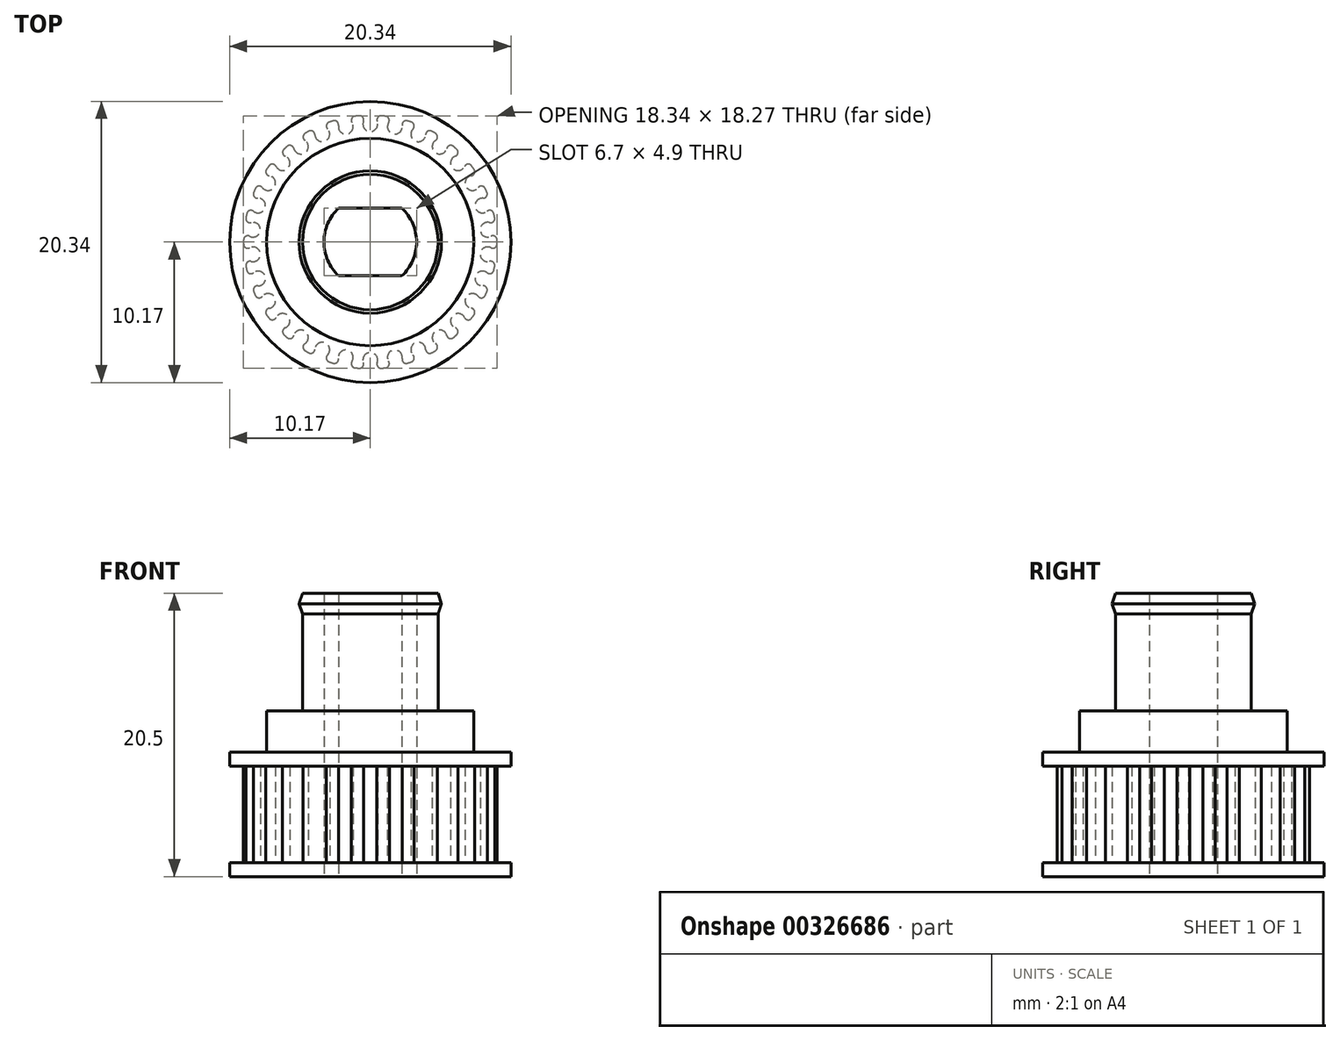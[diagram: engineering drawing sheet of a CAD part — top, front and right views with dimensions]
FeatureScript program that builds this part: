
annotation { "Feature Type Name" : "Feature", "Feature Type Description" : "" }
export const myFeature = defineFeature(function(context is Context, id is Id, definition is map)
    precondition{}
    {
        {
            assignVariable(context, id + "F0", {"name" : "e", "anyValue" : 3});
        }
        {
            assignVariable(context, id + "F1", {"name" : "h1", "anyValue" : 6});
        }
        {
            assignVariable(context, id + "F2", {"name" : "h2", "anyValue" : 6.5 + 5});
        }
        {
            var Q0;
            Q0=qCreatedBy(makeId("Top.planeOp"),FACE);
            var sketch = newSketch(context, id + "F3", { "sketchPlane" : qUnion([Q0])});
            skArc(sketch, "E0", {"start": v(-0.8, 9.13) * mm, "mid": v(0, -9.17) * mm, "end": v(0.8, 9.13) * mm, "construction": true});
            skCircle(sketch, "E1", {"center": v(0, 0) * mm, "radius": 7.5 * mm});
            skCircle(sketch, "E2", {"center": v(0, 0) * mm, "radius": 4.9 * mm});
            skArc(sketch, "E3", {"start": v(-2.28, 2.45) * mm, "mid": v(-3.35, 0) * mm, "end": v(-2.28, -2.45) * mm});
            skLineSegment(sketch, "E4.bottom", {"start": v(2.28, -2.45) * mm, "end": v(-2.28, -2.45) * mm});
            skLineSegment(sketch, "E4.top", {"start": v(2.28, 2.45) * mm, "end": v(-2.28, 2.45) * mm});
            skArc(sketch, "E5.trimOffspring", {"start": v(2.28, -2.45) * mm, "mid": v(3.35, 0) * mm, "end": v(2.28, 2.45) * mm});
            skPoint(sketch, "E6.orphan", {"position": v(3.35, 2.45) * mm});
            skPoint(sketch, "E7.orphan", {"position": v(3.35, -2.45) * mm});
            skPoint(sketch, "E8.orphan", {"position": v(-3.35, -2.45) * mm});
            skPoint(sketch, "E9.orphan", {"position": v(-3.35, 2.45) * mm});
            skLineSegment(sketch, "E10", {"start": v(0, 7.5) * mm, "end": v(0, 8) * mm, "construction": true});
            skCircle(sketch, "E11", {"center": v(0, 0) * mm, "radius": 10.17 * mm});
            skCircle(sketch, "E12", {"center": v(0, 0) * mm, "radius": 8 * mm, "construction": true});
            skLineSegment(sketch, "E13", {"start": v(0, 8) * mm, "end": v(0, 10.17) * mm});
            skArc(sketch, "E14", {"start": v(-0.5, 8.73) * mm, "mid": v(0, 8) * mm, "end": v(0.5, 8.73) * mm});
            skArc(sketch, "E15", {"start": v(0.8, 9.13) * mm, "mid": v(0.54, 9.01) * mm, "end": v(0.5, 8.73) * mm});
            skArc(sketch, "E16.MirrorCS", {"start": v(-0.8, 9.13) * mm, "mid": v(-0.54, 9.01) * mm, "end": v(-0.5, 8.73) * mm});
            skLineSegment(sketch, "E17", {"start": v(0, 0) * mm, "end": v(1.06, 10.11) * mm, "construction": true});
            skLineSegment(sketch, "E18", {"start": v(0, 0) * mm, "end": v(-1.06, 10.11) * mm, "construction": true});
            skArc(sketch, "E19", {"start": v(0.96, 9.12) * mm, "mid": v(0.88, 9.13) * mm, "end": v(0.8, 9.13) * mm});
            skArc(sketch, "E20.trimOffspring", {"start": v(-0.8, 9.13) * mm, "mid": v(-0.88, 9.13) * mm, "end": v(-0.96, 9.12) * mm});
            skArc(sketch, "E21.1.0", {"start": v(-2.69, 8.77) * mm, "mid": v(-2.76, 8.74) * mm, "end": v(-2.83, 8.72) * mm});
            skArc(sketch, "E21.1.1", {"start": v(-2.69, 8.77) * mm, "mid": v(-2.4, 8.7) * mm, "end": v(-2.3, 8.43) * mm});
            skArc(sketch, "E21.1.2", {"start": v(-2.3, 8.43) * mm, "mid": v(-1.66, 7.82) * mm, "end": v(-1.33, 8.64) * mm});
            skArc(sketch, "E21.1.3", {"start": v(-1.11, 9.1) * mm, "mid": v(-1.35, 8.93) * mm, "end": v(-1.33, 8.64) * mm});
            skArc(sketch, "E21.1.4", {"start": v(-0.96, 9.12) * mm, "mid": v(-1.04, 9.1) * mm, "end": v(-1.11, 9.1) * mm});
            skArc(sketch, "E21.2.0", {"start": v(-4.45, 8.02) * mm, "mid": v(-4.52, 7.98) * mm, "end": v(-4.58, 7.94) * mm});
            skArc(sketch, "E21.2.1", {"start": v(-4.45, 8.02) * mm, "mid": v(-4.16, 8.02) * mm, "end": v(-4, 7.77) * mm});
            skArc(sketch, "E21.2.2", {"start": v(-4, 7.77) * mm, "mid": v(-3.25, 7.3) * mm, "end": v(-3.1, 8.17) * mm});
            skArc(sketch, "E21.2.3", {"start": v(-2.98, 8.67) * mm, "mid": v(-3.17, 8.45) * mm, "end": v(-3.1, 8.17) * mm});
            skArc(sketch, "E21.2.4", {"start": v(-2.83, 8.72) * mm, "mid": v(-2.9, 8.7) * mm, "end": v(-2.98, 8.67) * mm});
            skArc(sketch, "E21.3.0", {"start": v(-6.02, 6.92) * mm, "mid": v(-6.08, 6.86) * mm, "end": v(-6.13, 6.81) * mm});
            skArc(sketch, "E21.3.1", {"start": v(-6.02, 6.92) * mm, "mid": v(-5.73, 6.98) * mm, "end": v(-5.53, 6.77) * mm});
            skArc(sketch, "E21.3.2", {"start": v(-5.53, 6.77) * mm, "mid": v(-4.7, 6.47) * mm, "end": v(-4.73, 7.35) * mm});
            skArc(sketch, "E21.3.3", {"start": v(-4.72, 7.86) * mm, "mid": v(-4.86, 7.6) * mm, "end": v(-4.73, 7.35) * mm});
            skArc(sketch, "E21.3.4", {"start": v(-4.58, 7.94) * mm, "mid": v(-4.65, 7.9) * mm, "end": v(-4.72, 7.86) * mm});
            skArc(sketch, "E21.4.0", {"start": v(-7.33, 5.51) * mm, "mid": v(-7.37, 5.45) * mm, "end": v(-7.42, 5.39) * mm});
            skArc(sketch, "E21.4.1", {"start": v(-7.33, 5.51) * mm, "mid": v(-7.06, 5.63) * mm, "end": v(-6.82, 5.47) * mm});
            skArc(sketch, "E21.4.2", {"start": v(-6.82, 5.47) * mm, "mid": v(-5.94, 5.35) * mm, "end": v(-6.15, 6.2) * mm});
            skArc(sketch, "E21.4.3", {"start": v(-6.25, 6.7) * mm, "mid": v(-6.34, 6.43) * mm, "end": v(-6.15, 6.2) * mm});
            skArc(sketch, "E21.4.4", {"start": v(-6.13, 6.81) * mm, "mid": v(-6.2, 6.76) * mm, "end": v(-6.25, 6.7) * mm});
            skArc(sketch, "E21.5.0", {"start": v(-8.31, 3.87) * mm, "mid": v(-8.34, 3.8) * mm, "end": v(-8.38, 3.73) * mm});
            skArc(sketch, "E21.5.1", {"start": v(-8.31, 3.87) * mm, "mid": v(-8.08, 4.04) * mm, "end": v(-7.8, 3.93) * mm});
            skArc(sketch, "E21.5.2", {"start": v(-7.8, 3.93) * mm, "mid": v(-6.93, 4) * mm, "end": v(-7.3, 4.8) * mm});
            skArc(sketch, "E21.5.3", {"start": v(-7.5, 5.26) * mm, "mid": v(-7.54, 4.97) * mm, "end": v(-7.3, 4.8) * mm});
            skArc(sketch, "E21.5.4", {"start": v(-7.42, 5.39) * mm, "mid": v(-7.46, 5.33) * mm, "end": v(-7.5, 5.26) * mm});
            skArc(sketch, "E21.6.0", {"start": v(-8.93, 2.06) * mm, "mid": v(-8.95, 1.98) * mm, "end": v(-8.97, 1.9) * mm});
            skArc(sketch, "E21.6.1", {"start": v(-8.93, 2.06) * mm, "mid": v(-8.74, 2.27) * mm, "end": v(-8.45, 2.22) * mm});
            skArc(sketch, "E21.6.2", {"start": v(-8.45, 2.22) * mm, "mid": v(-7.6, 2.47) * mm, "end": v(-8.14, 3.17) * mm});
            skArc(sketch, "E21.6.3", {"start": v(-8.44, 3.59) * mm, "mid": v(-8.4, 3.3) * mm, "end": v(-8.14, 3.17) * mm});
            skArc(sketch, "E21.6.4", {"start": v(-8.38, 3.73) * mm, "mid": v(-8.4, 3.66) * mm, "end": v(-8.44, 3.59) * mm});
            skArc(sketch, "E21.7.0", {"start": v(-9.17, 0.15) * mm, "mid": v(-9.17, 0.08) * mm, "end": v(-9.17, 0) * mm});
            skArc(sketch, "E21.7.1", {"start": v(-9.17, 0.15) * mm, "mid": v(-9.02, 0.4) * mm, "end": v(-8.73, 0.42) * mm});
            skArc(sketch, "E21.7.2", {"start": v(-8.73, 0.42) * mm, "mid": v(-7.95, 0.84) * mm, "end": v(-8.63, 1.4) * mm});
            skArc(sketch, "E21.7.3", {"start": v(-9, 1.75) * mm, "mid": v(-8.9, 1.48) * mm, "end": v(-8.63, 1.4) * mm});
            skArc(sketch, "E21.7.4", {"start": v(-8.97, 1.9) * mm, "mid": v(-8.98, 1.83) * mm, "end": v(-9, 1.75) * mm});
            skArc(sketch, "E21.8.0", {"start": v(-9, -1.75) * mm, "mid": v(-8.98, -1.83) * mm, "end": v(-8.97, -1.9) * mm});
            skArc(sketch, "E21.8.1", {"start": v(-9, -1.75) * mm, "mid": v(-8.9, -1.48) * mm, "end": v(-8.63, -1.4) * mm});
            skArc(sketch, "E21.8.2", {"start": v(-8.63, -1.4) * mm, "mid": v(-7.95, -0.84) * mm, "end": v(-8.73, -0.42) * mm});
            skArc(sketch, "E21.8.3", {"start": v(-9.17, -0.15) * mm, "mid": v(-9.02, -0.4) * mm, "end": v(-8.73, -0.42) * mm});
            skArc(sketch, "E21.8.4", {"start": v(-9.17, 0) * mm, "mid": v(-9.17, -0.08) * mm, "end": v(-9.17, -0.15) * mm});
            skArc(sketch, "E21.9.0", {"start": v(-8.44, -3.59) * mm, "mid": v(-8.4, -3.66) * mm, "end": v(-8.38, -3.73) * mm});
            skArc(sketch, "E21.9.1", {"start": v(-8.44, -3.59) * mm, "mid": v(-8.4, -3.3) * mm, "end": v(-8.14, -3.17) * mm});
            skArc(sketch, "E21.9.2", {"start": v(-8.14, -3.17) * mm, "mid": v(-7.6, -2.47) * mm, "end": v(-8.45, -2.22) * mm});
            skArc(sketch, "E21.9.3", {"start": v(-8.93, -2.06) * mm, "mid": v(-8.74, -2.27) * mm, "end": v(-8.45, -2.22) * mm});
            skArc(sketch, "E21.9.4", {"start": v(-8.97, -1.9) * mm, "mid": v(-8.95, -1.98) * mm, "end": v(-8.93, -2.06) * mm});
            skArc(sketch, "E21.10.0", {"start": v(-7.5, -5.26) * mm, "mid": v(-7.46, -5.33) * mm, "end": v(-7.42, -5.39) * mm});
            skArc(sketch, "E21.10.1", {"start": v(-7.5, -5.26) * mm, "mid": v(-7.54, -4.97) * mm, "end": v(-7.3, -4.8) * mm});
            skArc(sketch, "E21.10.2", {"start": v(-7.3, -4.8) * mm, "mid": v(-6.93, -4) * mm, "end": v(-7.8, -3.93) * mm});
            skArc(sketch, "E21.10.3", {"start": v(-8.31, -3.87) * mm, "mid": v(-8.08, -4.04) * mm, "end": v(-7.8, -3.93) * mm});
            skArc(sketch, "E21.10.4", {"start": v(-8.38, -3.73) * mm, "mid": v(-8.34, -3.8) * mm, "end": v(-8.31, -3.87) * mm});
            skArc(sketch, "E21.11.0", {"start": v(-6.25, -6.7) * mm, "mid": v(-6.2, -6.76) * mm, "end": v(-6.13, -6.81) * mm});
            skArc(sketch, "E21.11.1", {"start": v(-6.25, -6.7) * mm, "mid": v(-6.34, -6.43) * mm, "end": v(-6.15, -6.2) * mm});
            skArc(sketch, "E21.11.2", {"start": v(-6.15, -6.2) * mm, "mid": v(-5.94, -5.35) * mm, "end": v(-6.82, -5.47) * mm});
            skArc(sketch, "E21.11.3", {"start": v(-7.33, -5.51) * mm, "mid": v(-7.06, -5.63) * mm, "end": v(-6.82, -5.47) * mm});
            skArc(sketch, "E21.11.4", {"start": v(-7.42, -5.39) * mm, "mid": v(-7.37, -5.45) * mm, "end": v(-7.33, -5.51) * mm});
            skArc(sketch, "E21.12.0", {"start": v(-4.72, -7.86) * mm, "mid": v(-4.65, -7.9) * mm, "end": v(-4.58, -7.94) * mm});
            skArc(sketch, "E21.12.1", {"start": v(-4.72, -7.86) * mm, "mid": v(-4.86, -7.6) * mm, "end": v(-4.73, -7.35) * mm});
            skArc(sketch, "E21.12.2", {"start": v(-4.73, -7.35) * mm, "mid": v(-4.7, -6.47) * mm, "end": v(-5.53, -6.77) * mm});
            skArc(sketch, "E21.12.3", {"start": v(-6.02, -6.92) * mm, "mid": v(-5.73, -6.98) * mm, "end": v(-5.53, -6.77) * mm});
            skArc(sketch, "E21.12.4", {"start": v(-6.13, -6.81) * mm, "mid": v(-6.08, -6.86) * mm, "end": v(-6.02, -6.92) * mm});
            skArc(sketch, "E21.13.0", {"start": v(-2.98, -8.67) * mm, "mid": v(-2.9, -8.7) * mm, "end": v(-2.83, -8.72) * mm});
            skArc(sketch, "E21.13.1", {"start": v(-2.98, -8.67) * mm, "mid": v(-3.17, -8.45) * mm, "end": v(-3.1, -8.17) * mm});
            skArc(sketch, "E21.13.2", {"start": v(-3.1, -8.17) * mm, "mid": v(-3.25, -7.3) * mm, "end": v(-4, -7.77) * mm});
            skArc(sketch, "E21.13.3", {"start": v(-4.45, -8.02) * mm, "mid": v(-4.16, -8.02) * mm, "end": v(-4, -7.77) * mm});
            skArc(sketch, "E21.13.4", {"start": v(-4.58, -7.94) * mm, "mid": v(-4.52, -7.98) * mm, "end": v(-4.45, -8.02) * mm});
            skArc(sketch, "E21.14.0", {"start": v(-1.11, -9.1) * mm, "mid": v(-1.04, -9.1) * mm, "end": v(-0.96, -9.12) * mm});
            skArc(sketch, "E21.14.1", {"start": v(-1.11, -9.1) * mm, "mid": v(-1.35, -8.93) * mm, "end": v(-1.33, -8.64) * mm});
            skArc(sketch, "E21.14.2", {"start": v(-1.33, -8.64) * mm, "mid": v(-1.66, -7.82) * mm, "end": v(-2.3, -8.43) * mm});
            skArc(sketch, "E21.14.3", {"start": v(-2.69, -8.77) * mm, "mid": v(-2.4, -8.7) * mm, "end": v(-2.3, -8.43) * mm});
            skArc(sketch, "E21.14.4", {"start": v(-2.83, -8.72) * mm, "mid": v(-2.76, -8.74) * mm, "end": v(-2.69, -8.77) * mm});
            skArc(sketch, "E21.15.0", {"start": v(0.8, -9.13) * mm, "mid": v(0.88, -9.13) * mm, "end": v(0.96, -9.12) * mm});
            skArc(sketch, "E21.15.1", {"start": v(0.8, -9.13) * mm, "mid": v(0.54, -9.01) * mm, "end": v(0.5, -8.73) * mm});
            skArc(sketch, "E21.15.2", {"start": v(0.5, -8.73) * mm, "mid": v(0, -8) * mm, "end": v(-0.5, -8.73) * mm});
            skArc(sketch, "E21.15.3", {"start": v(-0.8, -9.13) * mm, "mid": v(-0.54, -9.01) * mm, "end": v(-0.5, -8.73) * mm});
            skArc(sketch, "E21.15.4", {"start": v(-0.96, -9.12) * mm, "mid": v(-0.88, -9.13) * mm, "end": v(-0.8, -9.13) * mm});
            skArc(sketch, "E21.16.0", {"start": v(2.69, -8.77) * mm, "mid": v(2.76, -8.74) * mm, "end": v(2.83, -8.72) * mm});
            skArc(sketch, "E21.16.1", {"start": v(2.69, -8.77) * mm, "mid": v(2.4, -8.7) * mm, "end": v(2.3, -8.43) * mm});
            skArc(sketch, "E21.16.2", {"start": v(2.3, -8.43) * mm, "mid": v(1.66, -7.82) * mm, "end": v(1.33, -8.64) * mm});
            skArc(sketch, "E21.16.3", {"start": v(1.11, -9.1) * mm, "mid": v(1.35, -8.93) * mm, "end": v(1.33, -8.64) * mm});
            skArc(sketch, "E21.16.4", {"start": v(0.96, -9.12) * mm, "mid": v(1.04, -9.1) * mm, "end": v(1.11, -9.1) * mm});
            skArc(sketch, "E21.17.0", {"start": v(4.45, -8.02) * mm, "mid": v(4.52, -7.98) * mm, "end": v(4.58, -7.94) * mm});
            skArc(sketch, "E21.17.1", {"start": v(4.45, -8.02) * mm, "mid": v(4.16, -8.02) * mm, "end": v(4, -7.77) * mm});
            skArc(sketch, "E21.17.2", {"start": v(4, -7.77) * mm, "mid": v(3.25, -7.3) * mm, "end": v(3.1, -8.17) * mm});
            skArc(sketch, "E21.17.3", {"start": v(2.98, -8.67) * mm, "mid": v(3.17, -8.45) * mm, "end": v(3.1, -8.17) * mm});
            skArc(sketch, "E21.17.4", {"start": v(2.83, -8.72) * mm, "mid": v(2.9, -8.7) * mm, "end": v(2.98, -8.67) * mm});
            skArc(sketch, "E21.18.0", {"start": v(6.02, -6.92) * mm, "mid": v(6.08, -6.86) * mm, "end": v(6.13, -6.81) * mm});
            skArc(sketch, "E21.18.1", {"start": v(6.02, -6.92) * mm, "mid": v(5.73, -6.98) * mm, "end": v(5.53, -6.77) * mm});
            skArc(sketch, "E21.18.2", {"start": v(5.53, -6.77) * mm, "mid": v(4.7, -6.47) * mm, "end": v(4.73, -7.35) * mm});
            skArc(sketch, "E21.18.3", {"start": v(4.72, -7.86) * mm, "mid": v(4.86, -7.6) * mm, "end": v(4.73, -7.35) * mm});
            skArc(sketch, "E21.18.4", {"start": v(4.58, -7.94) * mm, "mid": v(4.65, -7.9) * mm, "end": v(4.72, -7.86) * mm});
            skArc(sketch, "E21.19.0", {"start": v(7.33, -5.51) * mm, "mid": v(7.37, -5.45) * mm, "end": v(7.42, -5.39) * mm});
            skArc(sketch, "E21.19.1", {"start": v(7.33, -5.51) * mm, "mid": v(7.06, -5.63) * mm, "end": v(6.82, -5.47) * mm});
            skArc(sketch, "E21.19.2", {"start": v(6.82, -5.47) * mm, "mid": v(5.94, -5.35) * mm, "end": v(6.15, -6.2) * mm});
            skArc(sketch, "E21.19.3", {"start": v(6.25, -6.7) * mm, "mid": v(6.34, -6.43) * mm, "end": v(6.15, -6.2) * mm});
            skArc(sketch, "E21.19.4", {"start": v(6.13, -6.81) * mm, "mid": v(6.2, -6.76) * mm, "end": v(6.25, -6.7) * mm});
            skArc(sketch, "E21.20.0", {"start": v(8.31, -3.87) * mm, "mid": v(8.34, -3.8) * mm, "end": v(8.38, -3.73) * mm});
            skArc(sketch, "E21.20.1", {"start": v(8.31, -3.87) * mm, "mid": v(8.08, -4.04) * mm, "end": v(7.8, -3.93) * mm});
            skArc(sketch, "E21.20.2", {"start": v(7.8, -3.93) * mm, "mid": v(6.93, -4) * mm, "end": v(7.3, -4.8) * mm});
            skArc(sketch, "E21.20.3", {"start": v(7.5, -5.26) * mm, "mid": v(7.54, -4.97) * mm, "end": v(7.3, -4.8) * mm});
            skArc(sketch, "E21.20.4", {"start": v(7.42, -5.39) * mm, "mid": v(7.46, -5.33) * mm, "end": v(7.5, -5.26) * mm});
            skArc(sketch, "E21.21.0", {"start": v(8.93, -2.06) * mm, "mid": v(8.95, -1.98) * mm, "end": v(8.97, -1.9) * mm});
            skArc(sketch, "E21.21.1", {"start": v(8.93, -2.06) * mm, "mid": v(8.74, -2.27) * mm, "end": v(8.45, -2.22) * mm});
            skArc(sketch, "E21.21.2", {"start": v(8.45, -2.22) * mm, "mid": v(7.6, -2.47) * mm, "end": v(8.14, -3.17) * mm});
            skArc(sketch, "E21.21.3", {"start": v(8.44, -3.59) * mm, "mid": v(8.4, -3.3) * mm, "end": v(8.14, -3.17) * mm});
            skArc(sketch, "E21.21.4", {"start": v(8.38, -3.73) * mm, "mid": v(8.4, -3.66) * mm, "end": v(8.44, -3.59) * mm});
            skArc(sketch, "E21.22.0", {"start": v(9.17, -0.15) * mm, "mid": v(9.17, -0.08) * mm, "end": v(9.17, 0) * mm});
            skArc(sketch, "E21.22.1", {"start": v(9.17, -0.15) * mm, "mid": v(9.02, -0.4) * mm, "end": v(8.73, -0.42) * mm});
            skArc(sketch, "E21.22.2", {"start": v(8.73, -0.42) * mm, "mid": v(7.95, -0.84) * mm, "end": v(8.63, -1.4) * mm});
            skArc(sketch, "E21.22.3", {"start": v(9, -1.75) * mm, "mid": v(8.9, -1.48) * mm, "end": v(8.63, -1.4) * mm});
            skArc(sketch, "E21.22.4", {"start": v(8.97, -1.9) * mm, "mid": v(8.98, -1.83) * mm, "end": v(9, -1.75) * mm});
            skArc(sketch, "E21.23.0", {"start": v(9, 1.75) * mm, "mid": v(8.98, 1.83) * mm, "end": v(8.97, 1.9) * mm});
            skArc(sketch, "E21.23.1", {"start": v(9, 1.75) * mm, "mid": v(8.9, 1.48) * mm, "end": v(8.63, 1.4) * mm});
            skArc(sketch, "E21.23.2", {"start": v(8.63, 1.4) * mm, "mid": v(7.95, 0.84) * mm, "end": v(8.73, 0.42) * mm});
            skArc(sketch, "E21.23.3", {"start": v(9.17, 0.15) * mm, "mid": v(9.02, 0.4) * mm, "end": v(8.73, 0.42) * mm});
            skArc(sketch, "E21.23.4", {"start": v(9.17, 0) * mm, "mid": v(9.17, 0.08) * mm, "end": v(9.17, 0.15) * mm});
            skArc(sketch, "E21.24.0", {"start": v(8.44, 3.59) * mm, "mid": v(8.4, 3.66) * mm, "end": v(8.38, 3.73) * mm});
            skArc(sketch, "E21.24.1", {"start": v(8.44, 3.59) * mm, "mid": v(8.4, 3.3) * mm, "end": v(8.14, 3.17) * mm});
            skArc(sketch, "E21.24.2", {"start": v(8.14, 3.17) * mm, "mid": v(7.6, 2.47) * mm, "end": v(8.45, 2.22) * mm});
            skArc(sketch, "E21.24.3", {"start": v(8.93, 2.06) * mm, "mid": v(8.74, 2.27) * mm, "end": v(8.45, 2.22) * mm});
            skArc(sketch, "E21.24.4", {"start": v(8.97, 1.9) * mm, "mid": v(8.95, 1.98) * mm, "end": v(8.93, 2.06) * mm});
            skArc(sketch, "E21.25.0", {"start": v(7.5, 5.26) * mm, "mid": v(7.46, 5.33) * mm, "end": v(7.42, 5.39) * mm});
            skArc(sketch, "E21.25.1", {"start": v(7.5, 5.26) * mm, "mid": v(7.54, 4.97) * mm, "end": v(7.3, 4.8) * mm});
            skArc(sketch, "E21.25.2", {"start": v(7.3, 4.8) * mm, "mid": v(6.93, 4) * mm, "end": v(7.8, 3.93) * mm});
            skArc(sketch, "E21.25.3", {"start": v(8.31, 3.87) * mm, "mid": v(8.08, 4.04) * mm, "end": v(7.8, 3.93) * mm});
            skArc(sketch, "E21.25.4", {"start": v(8.38, 3.73) * mm, "mid": v(8.34, 3.8) * mm, "end": v(8.31, 3.87) * mm});
            skArc(sketch, "E21.26.0", {"start": v(6.25, 6.7) * mm, "mid": v(6.2, 6.76) * mm, "end": v(6.13, 6.81) * mm});
            skArc(sketch, "E21.26.1", {"start": v(6.25, 6.7) * mm, "mid": v(6.34, 6.43) * mm, "end": v(6.15, 6.2) * mm});
            skArc(sketch, "E21.26.2", {"start": v(6.15, 6.2) * mm, "mid": v(5.94, 5.35) * mm, "end": v(6.82, 5.47) * mm});
            skArc(sketch, "E21.26.3", {"start": v(7.33, 5.51) * mm, "mid": v(7.06, 5.63) * mm, "end": v(6.82, 5.47) * mm});
            skArc(sketch, "E21.26.4", {"start": v(7.42, 5.39) * mm, "mid": v(7.37, 5.45) * mm, "end": v(7.33, 5.51) * mm});
            skArc(sketch, "E21.27.0", {"start": v(4.72, 7.86) * mm, "mid": v(4.65, 7.9) * mm, "end": v(4.58, 7.94) * mm});
            skArc(sketch, "E21.27.1", {"start": v(4.72, 7.86) * mm, "mid": v(4.86, 7.6) * mm, "end": v(4.73, 7.35) * mm});
            skArc(sketch, "E21.27.2", {"start": v(4.73, 7.35) * mm, "mid": v(4.7, 6.47) * mm, "end": v(5.53, 6.77) * mm});
            skArc(sketch, "E21.27.3", {"start": v(6.02, 6.92) * mm, "mid": v(5.73, 6.98) * mm, "end": v(5.53, 6.77) * mm});
            skArc(sketch, "E21.27.4", {"start": v(6.13, 6.81) * mm, "mid": v(6.08, 6.86) * mm, "end": v(6.02, 6.92) * mm});
            skArc(sketch, "E21.28.0", {"start": v(2.98, 8.67) * mm, "mid": v(2.9, 8.7) * mm, "end": v(2.83, 8.72) * mm});
            skArc(sketch, "E21.28.1", {"start": v(2.98, 8.67) * mm, "mid": v(3.17, 8.45) * mm, "end": v(3.1, 8.17) * mm});
            skArc(sketch, "E21.28.2", {"start": v(3.1, 8.17) * mm, "mid": v(3.25, 7.3) * mm, "end": v(4, 7.77) * mm});
            skArc(sketch, "E21.28.3", {"start": v(4.45, 8.02) * mm, "mid": v(4.16, 8.02) * mm, "end": v(4, 7.77) * mm});
            skArc(sketch, "E21.28.4", {"start": v(4.58, 7.94) * mm, "mid": v(4.52, 7.98) * mm, "end": v(4.45, 8.02) * mm});
            skArc(sketch, "E21.29.0", {"start": v(1.11, 9.1) * mm, "mid": v(1.04, 9.1) * mm, "end": v(0.96, 9.12) * mm});
            skArc(sketch, "E21.29.1", {"start": v(1.11, 9.1) * mm, "mid": v(1.35, 8.93) * mm, "end": v(1.33, 8.64) * mm});
            skArc(sketch, "E21.29.2", {"start": v(1.33, 8.64) * mm, "mid": v(1.66, 7.82) * mm, "end": v(2.3, 8.43) * mm});
            skArc(sketch, "E21.29.3", {"start": v(2.69, 8.77) * mm, "mid": v(2.4, 8.7) * mm, "end": v(2.3, 8.43) * mm});
            skArc(sketch, "E21.29.4", {"start": v(2.83, 8.72) * mm, "mid": v(2.76, 8.74) * mm, "end": v(2.69, 8.77) * mm});
            skSolve(sketch);
        }
        {
            var Q0;
            Q0=makeQuery(id+"F3.imprint","IMPRINT",FACE,{"disambiguationData":[TD([[makeQuery(id+"F3.imprint","IMPRINT",EDGE,{"derivedFrom":sQuery(id+"F3.wireOp",EDGE,"E1")}),-1.0]])]});
            var Q1;
            Q1=makeQuery(id+"F3.imprint","IMPRINT",FACE,{"disambiguationData":[TD([[makeQuery(id+"F3.imprint","IMPRINT",EDGE,{"derivedFrom":sQuery(id+"F3.wireOp",EDGE,"E1")}),1.0]])]});
            var Q2;
            Q2=makeQuery(id+"F3.imprint","IMPRINT",FACE,{"disambiguationData":[TD([[makeQuery(id+"F3.imprint","IMPRINT",EDGE,{"derivedFrom":sQuery(id+"F3.wireOp",EDGE,"E2")}),1.0]])]});
            extrude(context, id + "F4", {"entities" : qUnion([Q0, Q1, Q2]), "depth" : 8 * mm});
        }
        {
            var Q0;
            Q0=makeQuery(id+"F3.imprint","IMPRINT",FACE,{"disambiguationData":[TD([[makeQuery(id+"F3.imprint","IMPRINT",EDGE,{"derivedFrom":sQuery(id+"F3.wireOp",EDGE,"E11")}),1.0]])]});
            var Q1;
            Q1=makeQuery(id+"F3.imprint","IMPRINT",FACE,{"disambiguationData":[TD([[makeQuery(id+"F3.imprint","IMPRINT",EDGE,{"derivedFrom":sQuery(id+"F3.wireOp",EDGE,"E1")}),-1.0]])]});
            var Q2;
            Q2=makeQuery(id+"F3.imprint","IMPRINT",FACE,{"disambiguationData":[TD([[makeQuery(id+"F3.imprint","IMPRINT",EDGE,{"derivedFrom":sQuery(id+"F3.wireOp",EDGE,"E1")}),1.0]])]});
            var Q3;
            Q3=makeQuery(id+"F3.imprint","IMPRINT",FACE,{"disambiguationData":[TD([[makeQuery(id+"F3.imprint","IMPRINT",EDGE,{"derivedFrom":sQuery(id+"F3.wireOp",EDGE,"E2")}),1.0]])]});
            extrude(context, id + "F5", {"entities" : qUnion([Q0, Q1, Q2, Q3]), "depth" : 1 * mm});
        }
        {
            var Q0;
            Q0=makeQuery(id+"F5.opExtrude","SWEPT_BODY",BODY,{"disambiguationData":[OSD([sQuery(id+"F3.wireOp",EDGE,"E11"),sQuery(id+"F3.wireOp",EDGE,"E14"),sQuery(id+"F3.wireOp",EDGE,"E15"),sQuery(id+"F3.wireOp",EDGE,"E16.MirrorCS"),sQuery(id+"F3.wireOp",EDGE,"E19"),sQuery(id+"F3.wireOp",EDGE,"E20.trimOffspring"),sQuery(id+"F3.wireOp",EDGE,"E21.1.0"),sQuery(id+"F3.wireOp",EDGE,"E21.1.1"),sQuery(id+"F3.wireOp",EDGE,"E21.1.2"),sQuery(id+"F3.wireOp",EDGE,"E21.1.3"),sQuery(id+"F3.wireOp",EDGE,"E21.1.4"),sQuery(id+"F3.wireOp",EDGE,"E21.2.0"),sQuery(id+"F3.wireOp",EDGE,"E21.2.1"),sQuery(id+"F3.wireOp",EDGE,"E21.2.2"),sQuery(id+"F3.wireOp",EDGE,"E21.2.3"),sQuery(id+"F3.wireOp",EDGE,"E21.2.4"),sQuery(id+"F3.wireOp",EDGE,"E21.3.0"),sQuery(id+"F3.wireOp",EDGE,"E21.3.1"),sQuery(id+"F3.wireOp",EDGE,"E21.3.2"),sQuery(id+"F3.wireOp",EDGE,"E21.3.3"),sQuery(id+"F3.wireOp",EDGE,"E21.3.4"),sQuery(id+"F3.wireOp",EDGE,"E21.4.0"),sQuery(id+"F3.wireOp",EDGE,"E21.4.1"),sQuery(id+"F3.wireOp",EDGE,"E21.4.2"),sQuery(id+"F3.wireOp",EDGE,"E21.4.3"),sQuery(id+"F3.wireOp",EDGE,"E21.4.4"),sQuery(id+"F3.wireOp",EDGE,"E21.5.0"),sQuery(id+"F3.wireOp",EDGE,"E21.5.1"),sQuery(id+"F3.wireOp",EDGE,"E21.5.2"),sQuery(id+"F3.wireOp",EDGE,"E21.5.3"),sQuery(id+"F3.wireOp",EDGE,"E21.5.4"),sQuery(id+"F3.wireOp",EDGE,"E21.6.0"),sQuery(id+"F3.wireOp",EDGE,"E21.6.1"),sQuery(id+"F3.wireOp",EDGE,"E21.6.2"),sQuery(id+"F3.wireOp",EDGE,"E21.6.3"),sQuery(id+"F3.wireOp",EDGE,"E21.6.4"),sQuery(id+"F3.wireOp",EDGE,"E21.7.0"),sQuery(id+"F3.wireOp",EDGE,"E21.7.1"),sQuery(id+"F3.wireOp",EDGE,"E21.7.2"),sQuery(id+"F3.wireOp",EDGE,"E21.7.3"),sQuery(id+"F3.wireOp",EDGE,"E21.7.4"),sQuery(id+"F3.wireOp",EDGE,"E21.8.0"),sQuery(id+"F3.wireOp",EDGE,"E21.8.1"),sQuery(id+"F3.wireOp",EDGE,"E21.8.2"),sQuery(id+"F3.wireOp",EDGE,"E21.8.3"),sQuery(id+"F3.wireOp",EDGE,"E21.8.4"),sQuery(id+"F3.wireOp",EDGE,"E21.9.0"),sQuery(id+"F3.wireOp",EDGE,"E21.9.1"),sQuery(id+"F3.wireOp",EDGE,"E21.9.2"),sQuery(id+"F3.wireOp",EDGE,"E21.9.3"),sQuery(id+"F3.wireOp",EDGE,"E21.9.4"),sQuery(id+"F3.wireOp",EDGE,"E21.10.0"),sQuery(id+"F3.wireOp",EDGE,"E21.10.1"),sQuery(id+"F3.wireOp",EDGE,"E21.10.2"),sQuery(id+"F3.wireOp",EDGE,"E21.10.3"),sQuery(id+"F3.wireOp",EDGE,"E21.10.4"),sQuery(id+"F3.wireOp",EDGE,"E21.11.0"),sQuery(id+"F3.wireOp",EDGE,"E21.11.1"),sQuery(id+"F3.wireOp",EDGE,"E21.11.2"),sQuery(id+"F3.wireOp",EDGE,"E21.11.3"),sQuery(id+"F3.wireOp",EDGE,"E21.11.4"),sQuery(id+"F3.wireOp",EDGE,"E21.12.0"),sQuery(id+"F3.wireOp",EDGE,"E21.12.1"),sQuery(id+"F3.wireOp",EDGE,"E21.12.2"),sQuery(id+"F3.wireOp",EDGE,"E21.12.3"),sQuery(id+"F3.wireOp",EDGE,"E21.12.4"),sQuery(id+"F3.wireOp",EDGE,"E21.13.0"),sQuery(id+"F3.wireOp",EDGE,"E21.13.1"),sQuery(id+"F3.wireOp",EDGE,"E21.13.2"),sQuery(id+"F3.wireOp",EDGE,"E21.13.3"),sQuery(id+"F3.wireOp",EDGE,"E21.13.4"),sQuery(id+"F3.wireOp",EDGE,"E21.14.0"),sQuery(id+"F3.wireOp",EDGE,"E21.14.1"),sQuery(id+"F3.wireOp",EDGE,"E21.14.2"),sQuery(id+"F3.wireOp",EDGE,"E21.14.3"),sQuery(id+"F3.wireOp",EDGE,"E21.14.4"),sQuery(id+"F3.wireOp",EDGE,"E21.15.0"),sQuery(id+"F3.wireOp",EDGE,"E21.15.1"),sQuery(id+"F3.wireOp",EDGE,"E21.15.2"),sQuery(id+"F3.wireOp",EDGE,"E21.15.3"),sQuery(id+"F3.wireOp",EDGE,"E21.15.4"),sQuery(id+"F3.wireOp",EDGE,"E21.16.0"),sQuery(id+"F3.wireOp",EDGE,"E21.16.1"),sQuery(id+"F3.wireOp",EDGE,"E21.16.2"),sQuery(id+"F3.wireOp",EDGE,"E21.16.3"),sQuery(id+"F3.wireOp",EDGE,"E21.16.4"),sQuery(id+"F3.wireOp",EDGE,"E21.17.0"),sQuery(id+"F3.wireOp",EDGE,"E21.17.1"),sQuery(id+"F3.wireOp",EDGE,"E21.17.2"),sQuery(id+"F3.wireOp",EDGE,"E21.17.3"),sQuery(id+"F3.wireOp",EDGE,"E21.17.4"),sQuery(id+"F3.wireOp",EDGE,"E21.18.0"),sQuery(id+"F3.wireOp",EDGE,"E21.18.1"),sQuery(id+"F3.wireOp",EDGE,"E21.18.2"),sQuery(id+"F3.wireOp",EDGE,"E21.18.3"),sQuery(id+"F3.wireOp",EDGE,"E21.18.4"),sQuery(id+"F3.wireOp",EDGE,"E21.19.0"),sQuery(id+"F3.wireOp",EDGE,"E21.19.1"),sQuery(id+"F3.wireOp",EDGE,"E21.19.2"),sQuery(id+"F3.wireOp",EDGE,"E21.19.3"),sQuery(id+"F3.wireOp",EDGE,"E21.19.4"),sQuery(id+"F3.wireOp",EDGE,"E21.20.0"),sQuery(id+"F3.wireOp",EDGE,"E21.20.1"),sQuery(id+"F3.wireOp",EDGE,"E21.20.2"),sQuery(id+"F3.wireOp",EDGE,"E21.20.3"),sQuery(id+"F3.wireOp",EDGE,"E21.20.4"),sQuery(id+"F3.wireOp",EDGE,"E21.21.0"),sQuery(id+"F3.wireOp",EDGE,"E21.21.1"),sQuery(id+"F3.wireOp",EDGE,"E21.21.2"),sQuery(id+"F3.wireOp",EDGE,"E21.21.3"),sQuery(id+"F3.wireOp",EDGE,"E21.21.4"),sQuery(id+"F3.wireOp",EDGE,"E21.22.0"),sQuery(id+"F3.wireOp",EDGE,"E21.22.1"),sQuery(id+"F3.wireOp",EDGE,"E21.22.2"),sQuery(id+"F3.wireOp",EDGE,"E21.22.3"),sQuery(id+"F3.wireOp",EDGE,"E21.22.4"),sQuery(id+"F3.wireOp",EDGE,"E21.23.0"),sQuery(id+"F3.wireOp",EDGE,"E21.23.1"),sQuery(id+"F3.wireOp",EDGE,"E21.23.2"),sQuery(id+"F3.wireOp",EDGE,"E21.23.3"),sQuery(id+"F3.wireOp",EDGE,"E21.23.4"),sQuery(id+"F3.wireOp",EDGE,"E21.24.0"),sQuery(id+"F3.wireOp",EDGE,"E21.24.1"),sQuery(id+"F3.wireOp",EDGE,"E21.24.2"),sQuery(id+"F3.wireOp",EDGE,"E21.24.3"),sQuery(id+"F3.wireOp",EDGE,"E21.24.4"),sQuery(id+"F3.wireOp",EDGE,"E21.25.0"),sQuery(id+"F3.wireOp",EDGE,"E21.25.1"),sQuery(id+"F3.wireOp",EDGE,"E21.25.2"),sQuery(id+"F3.wireOp",EDGE,"E21.25.3"),sQuery(id+"F3.wireOp",EDGE,"E21.25.4"),sQuery(id+"F3.wireOp",EDGE,"E21.26.0"),sQuery(id+"F3.wireOp",EDGE,"E21.26.1"),sQuery(id+"F3.wireOp",EDGE,"E21.26.2"),sQuery(id+"F3.wireOp",EDGE,"E21.26.3"),sQuery(id+"F3.wireOp",EDGE,"E21.26.4"),sQuery(id+"F3.wireOp",EDGE,"E21.27.0"),sQuery(id+"F3.wireOp",EDGE,"E21.27.1"),sQuery(id+"F3.wireOp",EDGE,"E21.27.2"),sQuery(id+"F3.wireOp",EDGE,"E21.27.3"),sQuery(id+"F3.wireOp",EDGE,"E21.27.4"),sQuery(id+"F3.wireOp",EDGE,"E21.28.0"),sQuery(id+"F3.wireOp",EDGE,"E21.28.1"),sQuery(id+"F3.wireOp",EDGE,"E21.28.2"),sQuery(id+"F3.wireOp",EDGE,"E21.28.3"),sQuery(id+"F3.wireOp",EDGE,"E21.28.4"),sQuery(id+"F3.wireOp",EDGE,"E21.29.0"),sQuery(id+"F3.wireOp",EDGE,"E21.29.1"),sQuery(id+"F3.wireOp",EDGE,"E21.29.2"),sQuery(id+"F3.wireOp",EDGE,"E21.29.3"),sQuery(id+"F3.wireOp",EDGE,"E21.29.4")])]});
            transform(context, id + "F6", {"entities" : qUnion([Q0]), "transformType" : TransformType.TRANSLATION_3D, "dx" : 0 * mm, "dy" : 0 * mm, "dz" : 8 * mm, "makeCopy" : true});
        }
        {
            var Q0;
            Q0=makeQuery(id+"F3.imprint","IMPRINT",FACE,{"disambiguationData":[TD([[makeQuery(id+"F3.imprint","IMPRINT",EDGE,{"derivedFrom":sQuery(id+"F3.wireOp",EDGE,"E1")}),1.0]])]});
            var Q1;
            Q1=makeQuery(id+"F3.imprint","IMPRINT",FACE,{"disambiguationData":[TD([[makeQuery(id+"F3.imprint","IMPRINT",EDGE,{"derivedFrom":sQuery(id+"F3.wireOp",EDGE,"E2")}),1.0]])]});
            extrude(context, id + "F7", {"entities" : qUnion([Q0, Q1]), "depth" : 12 * mm});
        }
        {
            var Q0;
            Q0=makeQuery(id+"F3.imprint","IMPRINT",FACE,{"disambiguationData":[TD([[makeQuery(id+"F3.imprint","IMPRINT",EDGE,{"derivedFrom":sQuery(id+"F3.wireOp",EDGE,"E2")}),1.0]])]});
            extrude(context, id + "F8", {"entities" : qUnion([Q0]), "operationType" : NewBodyOperationType.ADD, "depth" : (getVariable(context, 'e') + getVariable(context, 'h1') + getVariable(context, 'h2')) * mm});
        }
        {
            var Q0;
            Q0=qCreatedBy(makeId("Front.planeOp"),FACE);
            var sketch = newSketch(context, id + "F9", { "sketchPlane" : qUnion([Q0])});
            skLineSegment(sketch, "E22", {"start": v(0, 0) * mm, "end": v(0, 17.5) * mm, "construction": true});
            skLineSegment(sketch, "E23", {"start": v(-4.9, 6) * mm, "end": v(-4.9, 12.5) * mm});
            skLineSegment(sketch, "E24", {"start": v(4.9, 20.5) * mm, "end": v(4.9, 6) * mm});
            skLineSegment(sketch, "E25.bottom", {"start": v(4.9, 20.5) * mm, "end": v(5.15, 20.5) * mm, "construction": true});
            skLineSegment(sketch, "E25.top", {"start": v(4.9, 19) * mm, "end": v(5.15, 19) * mm, "construction": true});
            skLineSegment(sketch, "E25.left", {"start": v(4.9, 20.5) * mm, "end": v(4.9, 19) * mm, "construction": true});
            skLineSegment(sketch, "E25.right", {"start": v(5.15, 20.5) * mm, "end": v(5.15, 19) * mm, "construction": true});
            skPoint(sketch, "E26", {"position": v(5.15, 19.75) * mm});
            skLineSegment(sketch, "E27", {"start": v(4.9, 20.5) * mm, "end": v(5.15, 19.75) * mm});
            skLineSegment(sketch, "E28", {"start": v(5.15, 19.75) * mm, "end": v(4.9, 19) * mm});
            skLineSegment(sketch, "E29", {"start": v(4.9, 19) * mm, "end": v(4.9, 20.5) * mm});
            skSolve(sketch);
        }
        {
            var Q0;
            Q0=makeQuery(id+"F9.imprint","IMPRINT",FACE,{"disambiguationData":[TD([[makeQuery(id+"F9.imprint","IMPRINT",EDGE,{"derivedFrom":sQuery(id+"F9.wireOp",EDGE,"E27")}),-1.0]])]});
            var Q1;
            Q1=sQuery(id+"F9.wireOp",EDGE,"E22");
            revolve(context, id + "F10", {"operationType" : NewBodyOperationType.ADD, "entities" : qUnion([Q0]), "axis" : qUnion([Q1]), "revolveType" : RevolveType.FULL});
        }
        {
            var Q0;
            Q0=makeQuery(id+"F8.opExtrude","CAP_FACE",FACE,{"disambiguationData":[OSD([sQuery(id+"F3.wireOp",EDGE,"E2"),sQuery(id+"F3.wireOp",EDGE,"E3"),sQuery(id+"F3.wireOp",EDGE,"E4.bottom"),sQuery(id+"F3.wireOp",EDGE,"E4.top"),sQuery(id+"F3.wireOp",EDGE,"E5.trimOffspring")])],"isStart":false});
            cPlane(context, id + "F11", {"entities" : qUnion([Q0]), "cplaneType" : CPlaneType.OFFSET, "offset" : 0 * mm, "width" : 150 * mm, "height" : 150 * mm});
        }
        {
            var Q0;
            Q0=qCreatedBy(id+"F11.planeOp",FACE);
            var sketch = newSketch(context, id + "F12", { "sketchPlane" : qUnion([Q0])});
            skArc(sketch, "E30", {"start": v(-2.38, 2.7) * mm, "mid": v(-3.6, 0) * mm, "end": v(-2.38, -2.7) * mm});
            skLineSegment(sketch, "E31.bottom", {"start": v(-2.38, 2.7) * mm, "end": v(2.38, 2.7) * mm});
            skLineSegment(sketch, "E31.top", {"start": v(-2.38, -2.7) * mm, "end": v(2.38, -2.7) * mm});
            skPoint(sketch, "E32.orphan", {"position": v(4.18, 2.7) * mm});
            skPoint(sketch, "E33.orphan", {"position": v(3.52, -2.7) * mm});
            skArc(sketch, "E34.trimOffspring", {"start": v(2.38, -2.7) * mm, "mid": v(3.6, 0) * mm, "end": v(2.38, 2.7) * mm});
            skPoint(sketch, "E35.orphan", {"position": v(-4.18, -2.7) * mm});
            skPoint(sketch, "E36.orphan", {"position": v(-3.52, 2.7) * mm});
            skSolve(sketch);
        }
    });
